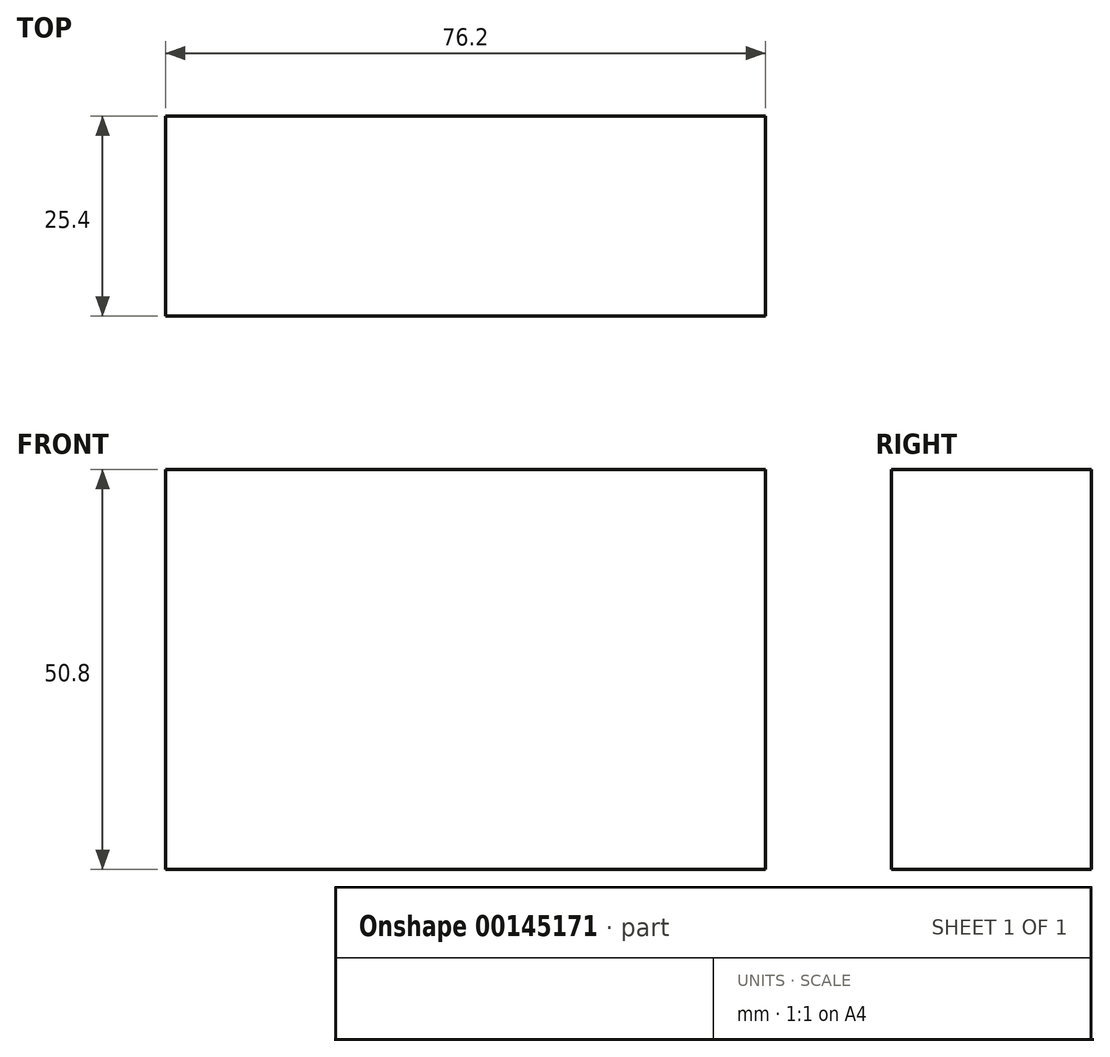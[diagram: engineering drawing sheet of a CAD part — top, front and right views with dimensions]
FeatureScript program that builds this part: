
annotation { "Feature Type Name" : "Feature", "Feature Type Description" : "" }
export const myFeature = defineFeature(function(context is Context, id is Id, definition is map)
    precondition{}
    {
        {
            var Q0;
            Q0=qCreatedBy(makeId("Front.planeOp"),FACE);
            var sketch = newSketch(context, id + "F0", { "sketchPlane" : qUnion([Q0])});
            skLineSegment(sketch, "E0.bottom", {"start": v(0, 0) * mm, "end": v(76.2, 0) * mm});
            skLineSegment(sketch, "E0.top", {"start": v(0, 50.8) * mm, "end": v(76.2, 50.8) * mm});
            skLineSegment(sketch, "E0.left", {"start": v(0, 0) * mm, "end": v(0, 50.8) * mm});
            skLineSegment(sketch, "E0.right", {"start": v(76.2, 0) * mm, "end": v(76.2, 50.8) * mm});
            skSolve(sketch);
        }
        {
            var Q0;
            Q0=makeQuery(id+"F0.imprint","IMPRINT",FACE,{"disambiguationData":[TD([[makeQuery(id+"F0.imprint","IMPRINT",EDGE,{"derivedFrom":sQuery(id+"F0.wireOp",EDGE,"E0.bottom")}),1.0]])]});
            extrude(context, id + "F1", {"entities" : qUnion([Q0]), "depth" : 25.4 * mm});
        }
    });
